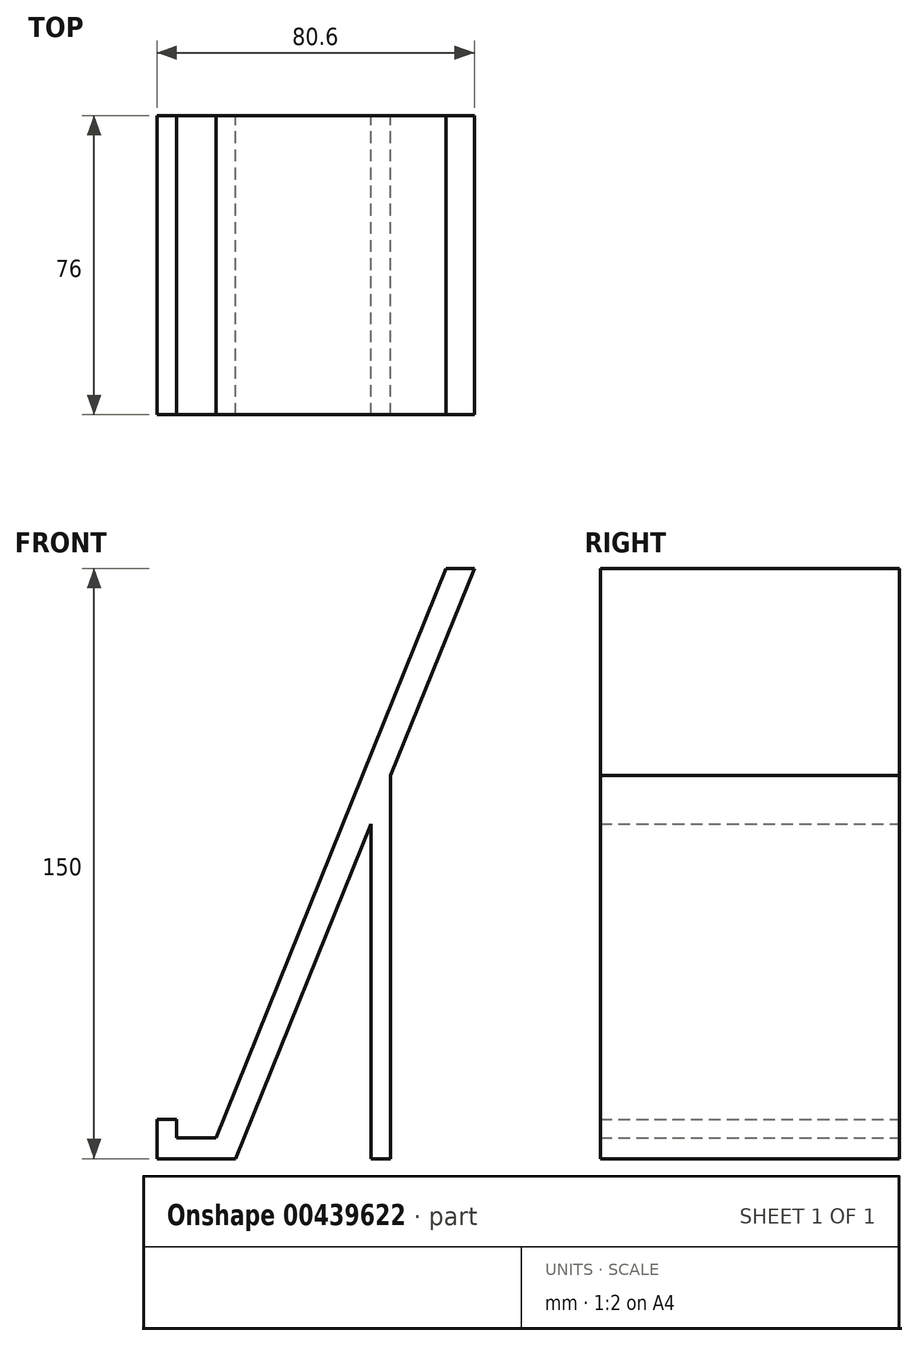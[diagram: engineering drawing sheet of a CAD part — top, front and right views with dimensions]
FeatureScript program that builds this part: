
annotation { "Feature Type Name" : "Feature", "Feature Type Description" : "" }
export const myFeature = defineFeature(function(context is Context, id is Id, definition is map)
    precondition{}
    {
        {
            var Q0;
            Q0=qCreatedBy(makeId("Front.planeOp"),FACE);
            var sketch = newSketch(context, id + "F0", { "sketchPlane" : qUnion([Q0])});
            skLineSegment(sketch, "E0", {"start": v(-54.34, 0) * mm, "end": v(-54.34, 10) * mm});
            skLineSegment(sketch, "E1", {"start": v(-54.34, 0) * mm, "end": v(-34.34, 0) * mm});
            skLineSegment(sketch, "E2", {"start": v(-49.34, 10) * mm, "end": v(-49.34, 5.3) * mm});
            skLineSegment(sketch, "E3", {"start": v(-39.34, 5.3) * mm, "end": v(-49.34, 5.3) * mm});
            skLineSegment(sketch, "E4", {"start": v(-39.34, 5.3) * mm, "end": v(19.12, 150) * mm});
            skLineSegment(sketch, "E5", {"start": v(-34.34, 0) * mm, "end": v(0, 85) * mm});
            skLineSegment(sketch, "E6", {"start": v(0, 85) * mm, "end": v(0, 0) * mm});
            skLineSegment(sketch, "E7", {"start": v(0, 0) * mm, "end": v(5, 0) * mm});
            skLineSegment(sketch, "E8", {"start": v(5, 0) * mm, "end": v(5, 97.38) * mm});
            skLineSegment(sketch, "E9", {"start": v(26.26, 150) * mm, "end": v(19.12, 150) * mm});
            skPoint(sketch, "E10.1.internal.orphan", {"position": v(-49.34, 10) * mm});
            skLineSegment(sketch, "E11", {"start": v(-54.34, 10) * mm, "end": v(-49.34, 10) * mm});
            skLineSegment(sketch, "E12.trimOffspring", {"start": v(5, 97.38) * mm, "end": v(26.26, 150) * mm});
            skSolve(sketch);
        }
        {
            var Q0;
            Q0=makeQuery(id+"F0.imprint","IMPRINT",FACE,{"disambiguationData":[TD([[makeQuery(id+"F0.imprint","IMPRINT",EDGE,{"derivedFrom":sQuery(id+"F0.wireOp",EDGE,"E0")}),-1.0]])]});
            extrude(context, id + "F1", {"entities" : qUnion([Q0]), "depth" : 76 * mm});
        }
    });
